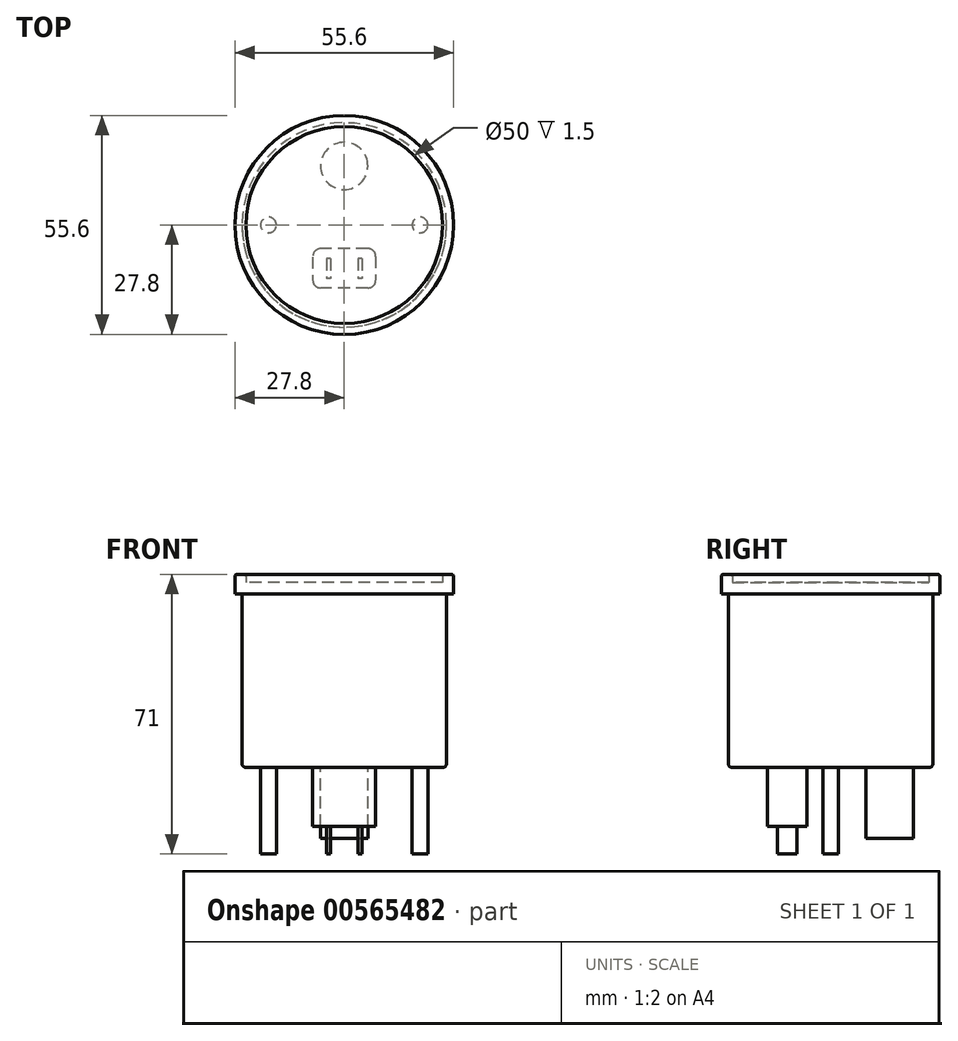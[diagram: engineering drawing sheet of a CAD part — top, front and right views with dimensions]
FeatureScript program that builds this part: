
annotation { "Feature Type Name" : "Feature", "Feature Type Description" : "" }
export const myFeature = defineFeature(function(context is Context, id is Id, definition is map)
    precondition{}
    {
        {
            var Q0;
            Q0=qCreatedBy(makeId("Top.planeOp"),FACE);
            var sketch = newSketch(context, id + "F0", { "sketchPlane" : qUnion([Q0])});
            skCircle(sketch, "E0", {"center": v(0, 0) * mm, "radius": 27.8 * mm});
            skCircle(sketch, "E1", {"center": v(0, 0) * mm, "radius": 25 * mm});
            skSolve(sketch);
        }
        {
            var Q0;
            Q0 = qSketchRegion(id + "F0", true);
            extrude(context, id + "F1", {"entities" : qUnion([Q0]), "depth" : 5 * mm, "offsetDistance" : 25 * mm});
        }
        {
            var Q0;
            Q0=qCreatedBy(makeId("Top.planeOp"),FACE);
            var sketch = newSketch(context, id + "F2", { "sketchPlane" : qUnion([Q0])});
            skCircle(sketch, "E2", {"center": v(0, 0) * mm, "radius": 25 * mm});
            skSolve(sketch);
        }
        {
            var Q0;
            Q0=makeQuery(id+"F2.imprint","IMPRINT",FACE,{"disambiguationData":[TD([[makeQuery(id+"F2.imprint","IMPRINT",EDGE,{"derivedFrom":sQuery(id+"F2.wireOp",EDGE,"E2")}),1.0]])]});
            extrude(context, id + "F3", {"entities" : qUnion([Q0]), "depth" : 3 * mm, "offsetDistance" : 25 * mm});
        }
        {
            var Q0;
            Q0=makeQuery(id+"F1.opExtrude","CAP_FACE",FACE,{"disambiguationData":[OSD([sQuery(id+"F0.wireOp",EDGE,"E0"),sQuery(id+"F0.wireOp",EDGE,"E1")])],"isStart":true});
            var sketch = newSketch(context, id + "F4", { "sketchPlane" : qUnion([Q0])});
            skCircle(sketch, "E3", {"center": v(0, 0) * mm, "radius": 26 * mm});
            skSolve(sketch);
        }
        {
            var Q0;
            Q0 = qSketchRegion(id + "F4", true);
            extrude(context, id + "F5", {"entities" : qUnion([Q0]), "operationType" : NewBodyOperationType.ADD, "depth" : 44 * mm, "offsetDistance" : 25 * mm});
        }
        {
            var Q0;
            Q0=makeQuery(id+"F5.opExtrude","CAP_EDGE",EDGE,{"disambiguationData":[OSD([sQuery(id+"F4.wireOp",EDGE,"E3")])],"isStart":false});
            fillet(context, id + "F6", {"entities" : qUnion([Q0]), "radius" : 1 * mm, "tangentPropagation" : true, "allowEdgeOverflow" : false});
        }
        {
            var Q0;
            Q0=makeQuery(id+"F5.opExtrude","CAP_FACE",FACE,{"disambiguationData":[OSD([sQuery(id+"F4.wireOp",EDGE,"E3")])],"isStart":false});
            var sketch = newSketch(context, id + "F7", { "sketchPlane" : qUnion([Q0])});
            skLineSegment(sketch, "E4", {"start": v(-39.14, 0) * mm, "end": v(48.61, 0) * mm, "construction": true});
            skCircle(sketch, "E5", {"center": v(-19.25, 0) * mm, "radius": 2 * mm});
            skCircle(sketch, "E6", {"center": v(19.25, 0) * mm, "radius": 2 * mm});
            skSolve(sketch);
        }
        {
            var Q0;
            Q0 = qSketchRegion(id + "F7", true);
            extrude(context, id + "F8", {"entities" : qUnion([Q0]), "depth" : 22 * mm, "offsetDistance" : 25 * mm});
        }
        {
            var Q0;
            Q0=makeQuery(id+"F5.opExtrude","CAP_FACE",FACE,{"disambiguationData":[OSD([sQuery(id+"F4.wireOp",EDGE,"E3")])],"isStart":false});
            var sketch = newSketch(context, id + "F9", { "sketchPlane" : qUnion([Q0])});
            skLineSegment(sketch, "E7", {"start": v(-34.02, 11) * mm, "end": v(40.71, 11) * mm, "construction": true});
            skLineSegment(sketch, "E8.bottom", {"start": v(6, 6) * mm, "end": v(-5.9, 6) * mm});
            skLineSegment(sketch, "E8.top", {"start": v(6, 16) * mm, "end": v(-6, 16) * mm});
            skLineSegment(sketch, "E8.left", {"start": v(8, 8) * mm, "end": v(8, 14) * mm});
            skLineSegment(sketch, "E8.right", {"start": v(-8, 8.1) * mm, "end": v(-8, 14) * mm});
            skPoint(sketch, "E8.middle", {"position": v(0, 11) * mm});
            skPoint(sketch, "E9.visualSharp", {"position": v(-8, 16) * mm});
            skArc(sketch, "E9.filletArc", {"start": v(-6, 16) * mm, "mid": v(-7.41, 15.4) * mm, "end": v(-8, 14) * mm});
            skPoint(sketch, "E10.visualSharp", {"position": v(8, 16) * mm});
            skArc(sketch, "E10.filletArc", {"start": v(8, 14) * mm, "mid": v(7.41, 15.4) * mm, "end": v(6, 16) * mm});
            skPoint(sketch, "E11.visualSharp", {"position": v(-8, 6) * mm});
            skArc(sketch, "E11.filletArc", {"start": v(-8, 8.1) * mm, "mid": v(-7.38, 6.62) * mm, "end": v(-5.9, 6) * mm});
            skPoint(sketch, "E12.visualSharp", {"position": v(8, 6) * mm});
            skArc(sketch, "E12.filletArc", {"start": v(6, 6) * mm, "mid": v(7.41, 6.6) * mm, "end": v(8, 8) * mm});
            skSolve(sketch);
        }
        {
            var Q0;
            Q0 = qSketchRegion(id + "F9", true);
            extrude(context, id + "F10", {"entities" : qUnion([Q0]), "depth" : 15 * mm, "offsetDistance" : 25 * mm});
        }
        {
            var Q0;
            Q0=makeQuery(id+"F5.opExtrude","CAP_FACE",FACE,{"disambiguationData":[OSD([sQuery(id+"F4.wireOp",EDGE,"E3")])],"isStart":false});
            var sketch = newSketch(context, id + "F11", { "sketchPlane" : qUnion([Q0])});
            skLineSegment(sketch, "E13", {"start": v(-35.67, -15) * mm, "end": v(42.83, -15) * mm, "construction": true});
            skCircle(sketch, "E14", {"center": v(0, -15) * mm, "radius": 6 * mm});
            skPoint(sketch, "E14.perimeterSnap0", {"position": v(3.58, -15) * mm});
            skSolve(sketch);
        }
        {
            var Q0;
            Q0=makeQuery(id+"F11.imprint","IMPRINT",FACE,{"disambiguationData":[TD([[makeQuery(id+"F11.imprint","IMPRINT",EDGE,{"derivedFrom":sQuery(id+"F11.wireOp",EDGE,"E14")}),1.0]])]});
            extrude(context, id + "F12", {"entities" : qUnion([Q0]), "depth" : 18 * mm, "offsetDistance" : 25 * mm});
        }
        {
            var Q0;
            Q0=makeQuery(id+"F10.opExtrude","CAP_FACE",FACE,{"disambiguationData":[OSD([sQuery(id+"F9.wireOp",EDGE,"E8.bottom"),sQuery(id+"F9.wireOp",EDGE,"E8.top"),sQuery(id+"F9.wireOp",EDGE,"E8.left"),sQuery(id+"F9.wireOp",EDGE,"E8.right"),sQuery(id+"F9.wireOp",EDGE,"E9.filletArc"),sQuery(id+"F9.wireOp",EDGE,"E10.filletArc"),sQuery(id+"F9.wireOp",EDGE,"E11.filletArc"),sQuery(id+"F9.wireOp",EDGE,"E12.filletArc")])],"isStart":false});
            var sketch = newSketch(context, id + "F13", { "sketchPlane" : qUnion([Q0])});
            skLineSegment(sketch, "E15", {"start": v(-8, 11.05) * mm, "end": v(8, 11.05) * mm, "construction": true});
            skLineSegment(sketch, "E16.bottom", {"start": v(-3.5, 8.55) * mm, "end": v(-4.5, 8.55) * mm});
            skLineSegment(sketch, "E16.top", {"start": v(-3.5, 13.55) * mm, "end": v(-4.5, 13.55) * mm});
            skLineSegment(sketch, "E16.left", {"start": v(-3.5, 8.55) * mm, "end": v(-3.5, 13.55) * mm});
            skLineSegment(sketch, "E16.right", {"start": v(-4.5, 8.55) * mm, "end": v(-4.5, 13.55) * mm});
            skPoint(sketch, "E16.middle", {"position": v(-4, 11.05) * mm});
            skLineSegment(sketch, "E17.bottom", {"start": v(4.5, 8.55) * mm, "end": v(3.5, 8.55) * mm});
            skLineSegment(sketch, "E17.top", {"start": v(4.5, 13.55) * mm, "end": v(3.5, 13.55) * mm});
            skLineSegment(sketch, "E17.left", {"start": v(4.5, 8.55) * mm, "end": v(4.5, 13.55) * mm});
            skLineSegment(sketch, "E17.right", {"start": v(3.5, 8.55) * mm, "end": v(3.5, 13.55) * mm});
            skPoint(sketch, "E17.middle", {"position": v(4, 11.05) * mm});
            skSolve(sketch);
        }
        {
            var Q0;
            Q0 = qSketchRegion(id + "F13", true);
            extrude(context, id + "F14", {"entities" : qUnion([Q0]), "operationType" : NewBodyOperationType.ADD, "depth" : 7 * mm, "offsetDistance" : 25 * mm});
        }
        {
            var Q0;
            Q0=makeQuery(id+"F1.opExtrude","CAP_EDGE",EDGE,{"disambiguationData":[OSD([sQuery(id+"F0.wireOp",EDGE,"E0")])],"isStart":false});
            var Q1;
            Q1=makeQuery(id+"F1.opExtrude","CAP_EDGE",EDGE,{"disambiguationData":[OSD([sQuery(id+"F0.wireOp",EDGE,"E1")])],"isStart":false});
            fillet(context, id + "F15", {"entities" : qUnion([Q0, Q1]), "radius" : .5 * mm, "tangentPropagation" : true, "allowEdgeOverflow" : false});
        }
    });
